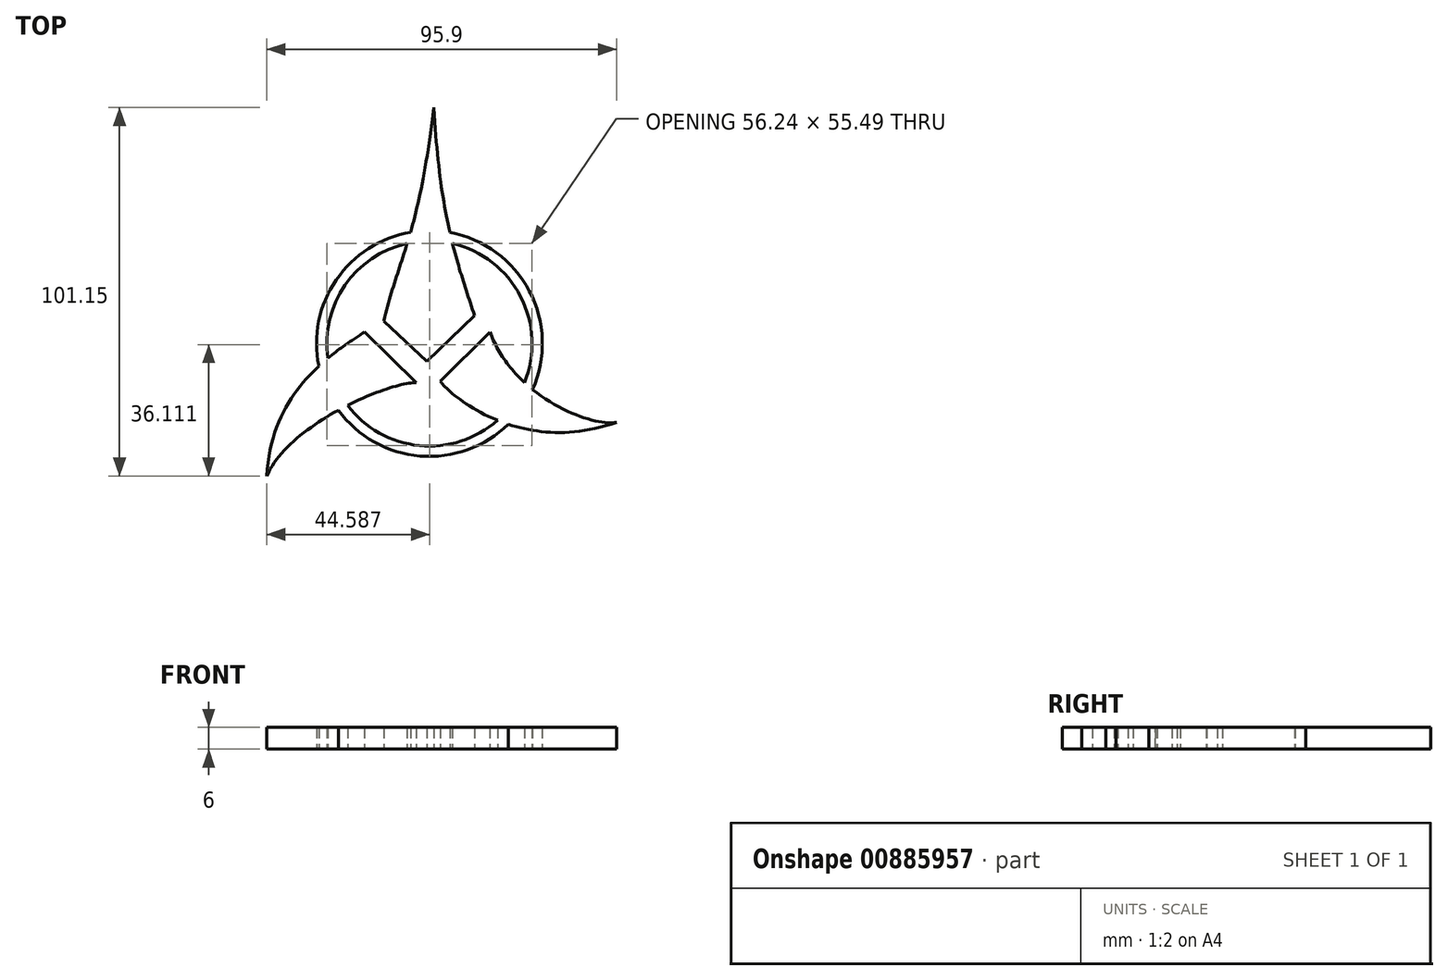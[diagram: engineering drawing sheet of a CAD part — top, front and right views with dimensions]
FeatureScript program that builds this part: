
annotation { "Feature Type Name" : "Feature", "Feature Type Description" : "" }
export const myFeature = defineFeature(function(context is Context, id is Id, definition is map)
    precondition{}
    {
        {
            var Q0;
            Q0=qCreatedBy(makeId("Top.planeOp"),FACE);
            var sketch = newSketch(context, id + "F0", { "sketchPlane" : qUnion([Q0])});
            skLineSegment(sketch, "E0.bottom", {"start": v(26, -26) * mm, "end": v(-26, -26) * mm});
            skLineSegment(sketch, "E0.top", {"start": v(26, 26) * mm, "end": v(-26, 26) * mm});
            skLineSegment(sketch, "E0.left", {"start": v(26, -26) * mm, "end": v(26, 26) * mm});
            skLineSegment(sketch, "E0.right", {"start": v(-26, -26) * mm, "end": v(-26, 26) * mm});
            skPoint(sketch, "E0.middle", {"position": v(0, 0) * mm});
            skFitSpline(sketch, "E1", {"points": [v(5.58, -3.14) * mm, v(0, 25.42) * mm], "startDerivative": vector(-7.97, 24.3) * mm, "endDerivative": vector(-2.68, 44.76) * mm});
            skLineSegment(sketch, "E2", {"start": v(5.58, -3.14) * mm, "end": v(-0.98, -9.4) * mm});
            skLineSegment(sketch, "E3", {"start": v(-0.98, -9.4) * mm, "end": v(-6.88, -3.86) * mm});
            skFitSpline(sketch, "E4", {"points": [v(-6.88, -3.86) * mm, v(0, 25.42) * mm], "startDerivative": vector(6, 25.38) * mm, "endDerivative": vector(6.17, 52.43) * mm});
            skFitSpline(sketch, "E5", {"points": [v(7.71, -5.4) * mm, v(25.06, -17.77) * mm], "startDerivative": vector(10.81, -28.76) * mm, "endDerivative": vector(7.96, 2.03) * mm});
            skFitSpline(sketch, "E6", {"points": [v(25.06, -17.77) * mm, v(0.9, -12.12) * mm], "startDerivative": vector(-42.04, -14.94) * mm, "endDerivative": vector(-0.74, 2.3) * mm});
            skFitSpline(sketch, "E7", {"points": [v(-2.4, -12.35) * mm, v(-22.9, -25.15) * mm], "startDerivative": vector(-10.99, 0.48) * mm, "endDerivative": vector(-8.98, -21.45) * mm});
            skFitSpline(sketch, "E8", {"points": [v(-9.54, -5.35) * mm, v(-22.9, -25.15) * mm], "startDerivative": vector(-7.93, -6.25) * mm, "endDerivative": vector(-1.72, -38.18) * mm});
            skLineSegment(sketch, "E9", {"start": v(-9.54, -5.35) * mm, "end": v(-2.4, -12.35) * mm});
            skLineSegment(sketch, "E10", {"start": v(0.9, -12.12) * mm, "end": v(7.71, -5.4) * mm});
            skCircle(sketch, "E11", {"center": v(-0.6, -6.96) * mm, "radius": 15.5 * mm});
            skCircle(sketch, "E12.0", {"center": v(-0.6, -6.96) * mm, "radius": 14.07 * mm});
            skSolve(sketch);
        }
        {
            var Q0;
            {var subQ0=sQuery(id+"F0.wireOp",EDGE,"E12.0");var subQ1=sQuery(id+"F0.wireOp",EDGE,"E1");var subQ2=makeQuery(id+"F0.imprint","INTERSECT",VERTEX,{"derivedFrom":[subQ1,subQ0]});Q0=makeQuery(id+"F0.imprint","IMPRINT",FACE,{"disambiguationData":[TD([[makeQuery(id+"F0.imprint","IMPRINT",EDGE,{"disambiguationData":[TD([[subQ2,-1.0]])],"derivedFrom":subQ1}),1.0]])]});}
            var Q1;
            {var subQ0=sQuery(id+"F0.wireOp",EDGE,"E4");var subQ1=sQuery(id+"F0.wireOp",EDGE,"E1");var subQ2=makeQuery(id+"F0.imprint","INTERSECT",VERTEX,{"derivedFrom":[subQ1,subQ0]});Q1=makeQuery(id+"F0.imprint","IMPRINT",FACE,{"disambiguationData":[TD([[makeQuery(id+"F0.imprint","IMPRINT",EDGE,{"disambiguationData":[TD([[subQ2,1.0]])],"derivedFrom":subQ1}),1.0]])]});}
            var Q2;
            {var subQ1=sQuery(id+"F0.wireOp",EDGE,"E2");Q2=makeQuery(id+"F0.imprint","IMPRINT",FACE,{"disambiguationData":[TD([[makeQuery(id+"F0.imprint","IMPRINT",EDGE,{"derivedFrom":subQ1}),-1.0]])]});}
            var Q3;
            {var subQ0=sQuery(id+"F0.wireOp",EDGE,"E10");Q3=makeQuery(id+"F0.imprint","IMPRINT",FACE,{"disambiguationData":[TD([[makeQuery(id+"F0.imprint","IMPRINT",EDGE,{"derivedFrom":subQ0}),-1.0]])]});}
            var Q4;
            {var subQ0=sQuery(id+"F0.wireOp",EDGE,"E9");Q4=makeQuery(id+"F0.imprint","IMPRINT",FACE,{"disambiguationData":[TD([[makeQuery(id+"F0.imprint","IMPRINT",EDGE,{"derivedFrom":subQ0}),-1.0]])]});}
            var Q5;
            {var subQ0=sQuery(id+"F0.wireOp",EDGE,"E8");var subQ1=sQuery(id+"F0.wireOp",EDGE,"E7");var subQ2=makeQuery(id+"F0.imprint","INTERSECT",VERTEX,{"derivedFrom":[subQ1,subQ0]});Q5=makeQuery(id+"F0.imprint","IMPRINT",FACE,{"disambiguationData":[TD([[makeQuery(id+"F0.imprint","IMPRINT",EDGE,{"disambiguationData":[TD([[subQ2,1.0]])],"derivedFrom":subQ1}),-1.0]])]});}
            var Q6;
            {var subQ0=sQuery(id+"F0.wireOp",EDGE,"E6");var subQ1=sQuery(id+"F0.wireOp",EDGE,"E5");var subQ2=makeQuery(id+"F0.imprint","INTERSECT",VERTEX,{"derivedFrom":[subQ1,subQ0]});Q6=makeQuery(id+"F0.imprint","IMPRINT",FACE,{"disambiguationData":[TD([[makeQuery(id+"F0.imprint","IMPRINT",EDGE,{"disambiguationData":[TD([[subQ2,1.0]])],"derivedFrom":subQ1}),-1.0]])]});}
            var Q7;
            {var subQ0=sQuery(id+"F0.wireOp",EDGE,"E12.0");var subQ1=sQuery(id+"F0.wireOp",EDGE,"E7");var subQ2=makeQuery(id+"F0.imprint","INTERSECT",VERTEX,{"derivedFrom":[subQ1,subQ0]});Q7=makeQuery(id+"F0.imprint","IMPRINT",FACE,{"disambiguationData":[TD([[makeQuery(id+"F0.imprint","IMPRINT",EDGE,{"disambiguationData":[TD([[subQ2,-1.0]])],"derivedFrom":subQ1}),-1.0]])]});}
            var Q8;
            {var subQ0=sQuery(id+"F0.wireOp",EDGE,"E12.0");var subQ1=sQuery(id+"F0.wireOp",EDGE,"E5");var subQ2=makeQuery(id+"F0.imprint","INTERSECT",VERTEX,{"derivedFrom":[subQ1,subQ0]});Q8=makeQuery(id+"F0.imprint","IMPRINT",FACE,{"disambiguationData":[TD([[makeQuery(id+"F0.imprint","IMPRINT",EDGE,{"disambiguationData":[TD([[subQ2,-1.0]])],"derivedFrom":subQ1}),-1.0]])]});}
            var Q9;
            {var subQ0=sQuery(id+"F0.wireOp",EDGE,"E12.0");var subQ1=sQuery(id+"F0.wireOp",EDGE,"E1");var subQ2=makeQuery(id+"F0.imprint","INTERSECT",VERTEX,{"derivedFrom":[subQ1,subQ0]});Q9=makeQuery(id+"F0.imprint","IMPRINT",FACE,{"disambiguationData":[TD([[makeQuery(id+"F0.imprint","IMPRINT",EDGE,{"disambiguationData":[TD([[subQ2,-1.0]])],"derivedFrom":subQ1}),-1.0]])]});}
            var Q10;
            {var subQ0=sQuery(id+"F0.wireOp",EDGE,"E12.0");var subQ1=sQuery(id+"F0.wireOp",EDGE,"E4");var subQ2=makeQuery(id+"F0.imprint","INTERSECT",VERTEX,{"derivedFrom":[subQ1,subQ0]});Q10=makeQuery(id+"F0.imprint","IMPRINT",FACE,{"disambiguationData":[TD([[makeQuery(id+"F0.imprint","IMPRINT",EDGE,{"disambiguationData":[TD([[subQ2,-1.0]])],"derivedFrom":subQ1}),1.0]])]});}
            var Q11;
            {var subQ0=sQuery(id+"F0.wireOp",EDGE,"E11");var subQ1=sQuery(id+"F0.wireOp",EDGE,"E6");var subQ2=makeQuery(id+"F0.imprint","INTERSECT",VERTEX,{"derivedFrom":[subQ1,subQ0]});Q11=makeQuery(id+"F0.imprint","IMPRINT",FACE,{"disambiguationData":[TD([[makeQuery(id+"F0.imprint","IMPRINT",EDGE,{"disambiguationData":[TD([[subQ2,-1.0]])],"derivedFrom":subQ1}),1.0]])]});}
            extrude(context, id + "F1", {"entities" : qUnion([Q0, Q1, Q2, Q3, Q4, Q5, Q6, Q7, Q8, Q9, Q10, Q11]), "depth" : 3 * mm, "offsetDistance" : 25 * mm});
        }
        {
            var Q0;
            Q0=makeQuery(id+"F1.opExtrude","SWEPT_BODY",BODY,{"disambiguationData":[OSD([sQuery(id+"F0.wireOp",EDGE,"E1"),sQuery(id+"F0.wireOp",EDGE,"E2"),sQuery(id+"F0.wireOp",EDGE,"E3"),sQuery(id+"F0.wireOp",EDGE,"E4"),sQuery(id+"F0.wireOp",EDGE,"E5"),sQuery(id+"F0.wireOp",EDGE,"E6"),sQuery(id+"F0.wireOp",EDGE,"E7"),sQuery(id+"F0.wireOp",EDGE,"E8"),sQuery(id+"F0.wireOp",EDGE,"E9"),sQuery(id+"F0.wireOp",EDGE,"E10"),sQuery(id+"F0.wireOp",EDGE,"E11"),sQuery(id+"F0.wireOp",EDGE,"E12.0")])]});
            var Q1;
            Q1=sQuery(id+"F0.wireOp",VERTEX,"E2.end");
            transform(context, id + "F2", {"entities" : qUnion([Q0]), "transformType" : TransformType.SCALE_UNIFORMLY, "scale" : 2, "scalePoint" : qUnion([Q1]), "makeCopy" : false});
        }
    });
